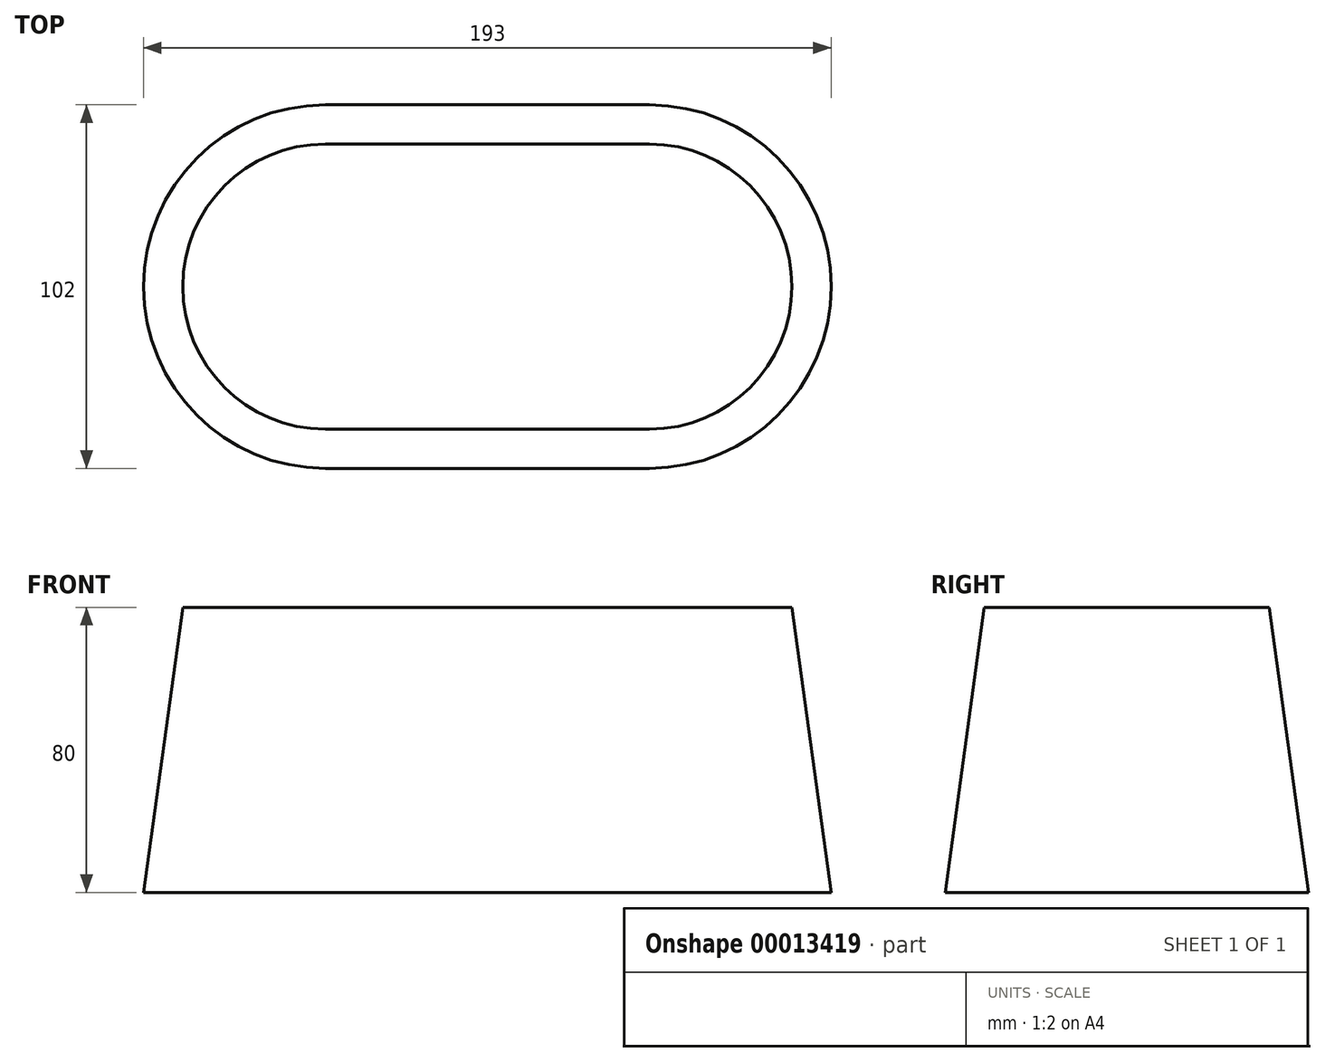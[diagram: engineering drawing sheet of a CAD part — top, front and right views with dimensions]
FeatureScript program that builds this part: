
annotation { "Feature Type Name" : "Feature", "Feature Type Description" : "" }
export const myFeature = defineFeature(function(context is Context, id is Id, definition is map)
    precondition{}
    {
        {
            var Q0;
            Q0=qCreatedBy(makeId("Top.planeOp"),FACE);
            var sketch = newSketch(context, id + "F0", { "sketchPlane" : qUnion([Q0])});
            skArc(sketch, "E0", {"start": v(-91, 51) * mm, "mid": v(-142, 0) * mm, "end": v(-91, -51) * mm});
            skArc(sketch, "E1", {"start": v(0, -51) * mm, "mid": v(51, 0) * mm, "end": v(0, 51) * mm});
            skLineSegment(sketch, "E2", {"start": v(0, 51) * mm, "end": v(-91, 51) * mm});
            skLineSegment(sketch, "E3", {"start": v(0, -51) * mm, "end": v(-91, -51) * mm});
            skSolve(sketch);
        }
        {
            var Q0;
            Q0=makeQuery(id+"F0.imprint","IMPRINT",FACE,{"disambiguationData":[TD([[makeQuery(id+"F0.imprint","IMPRINT",EDGE,{"derivedFrom":sQuery(id+"F0.wireOp",EDGE,"E0")}),1.0]])]});
            cPlane(context, id + "F1", {"entities" : qUnion([Q0]), "cplaneType" : CPlaneType.OFFSET, "offset" : 80 * mm, "width" : 150 * mm, "height" : 150 * mm});
        }
        {
            var Q0;
            Q0=qCreatedBy(id+"F1.planeOp",FACE);
            var sketch = newSketch(context, id + "F2", { "sketchPlane" : qUnion([Q0])});
            skArc(sketch, "E4.0", {"start": v(-91, 40) * mm, "mid": v(-131, 0) * mm, "end": v(-91, -40) * mm});
            skLineSegment(sketch, "E4.1", {"start": v(0, 40) * mm, "end": v(-91, 40) * mm});
            skArc(sketch, "E4.2", {"start": v(0, -40) * mm, "mid": v(40, 0) * mm, "end": v(0, 40) * mm});
            skLineSegment(sketch, "E4.3", {"start": v(0, -40) * mm, "end": v(-91, -40) * mm});
            skSolve(sketch);
        }
        {
            var Q0;
            Q0=makeQuery(id+"F0.imprint","IMPRINT",FACE,{"disambiguationData":[TD([[makeQuery(id+"F0.imprint","IMPRINT",EDGE,{"derivedFrom":sQuery(id+"F0.wireOp",EDGE,"E0")}),1.0]])]});
            var Q1;
            Q1=makeQuery(id+"F2.imprint","IMPRINT",FACE,{"disambiguationData":[TD([[makeQuery(id+"F2.imprint","IMPRINT",EDGE,{"derivedFrom":sQuery(id+"F2.wireOp",EDGE,"E4.0")}),1.0]])]});
            loft(context, id + "F3", {"sheetProfilesArray" : [{ "sheetProfileEntities" : qUnion([Q0]) }, { "sheetProfileEntities" : qUnion([Q1]) }]});
        }
    });
